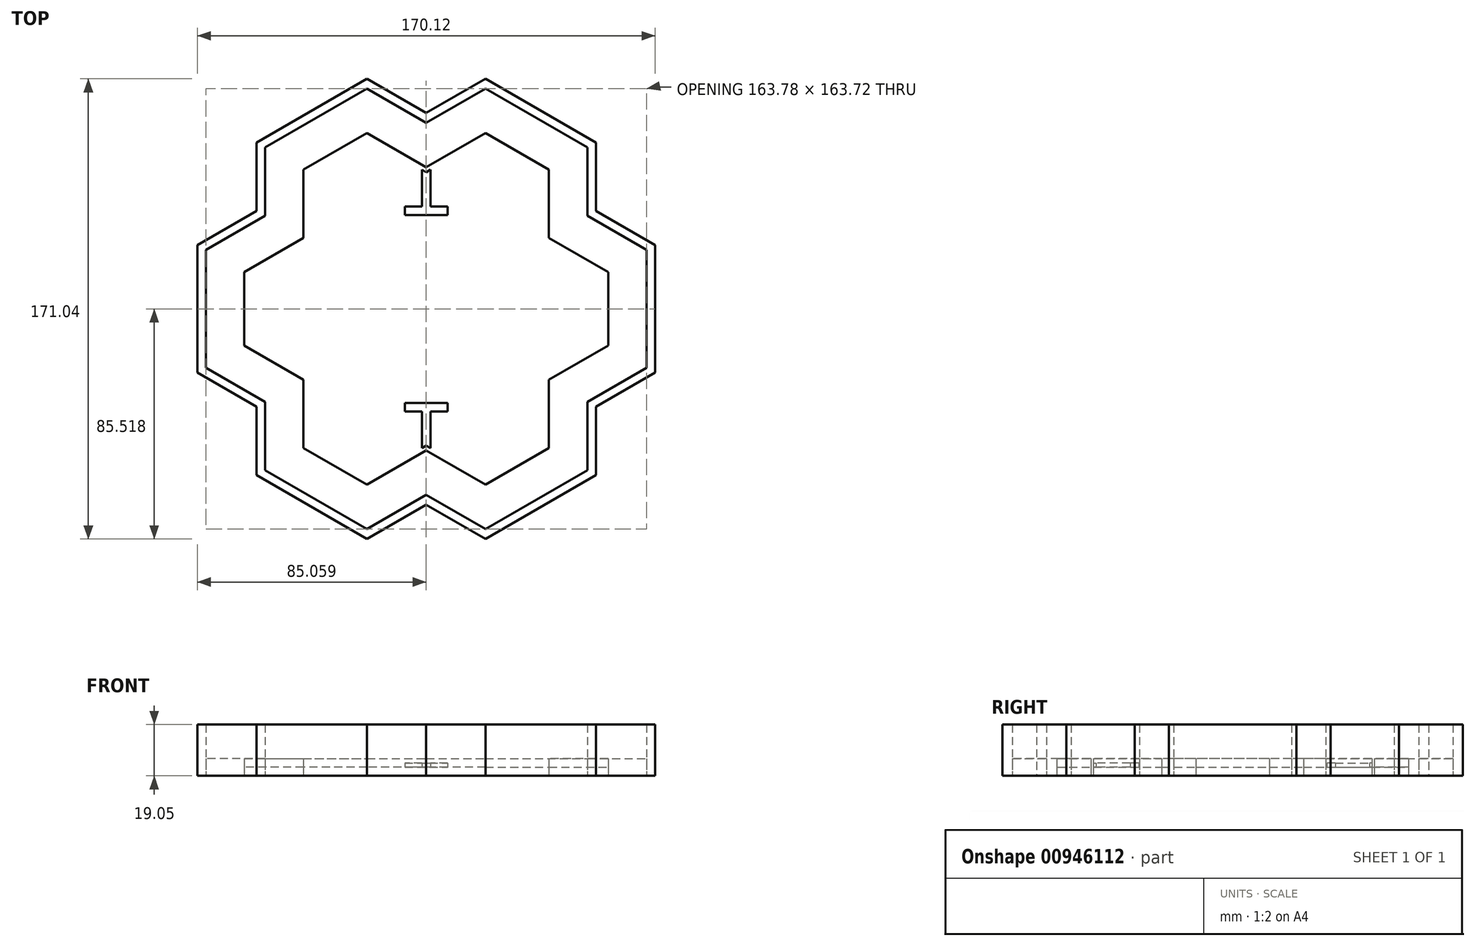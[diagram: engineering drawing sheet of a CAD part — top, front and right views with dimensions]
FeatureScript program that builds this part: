
annotation { "Feature Type Name" : "Feature", "Feature Type Description" : "" }
export const myFeature = defineFeature(function(context is Context, id is Id, definition is map)
    precondition{}
    {
        {
            var Q0;
            Q0=qCreatedBy(makeId("Top.planeOp"),FACE);
            var sketch = newSketch(context, id + "F0", { "sketchPlane" : qUnion([Q0])});
            skLineSegment(sketch, "E0.MirrorCS", {"start": v(-44.94, 24.68) * mm, "end": v(-66.93, 11.98) * mm});
            skLineSegment(sketch, "E1.MirrorCS", {"start": v(-66.93, 11.98) * mm, "end": v(-66.93, -13.42) * mm});
            skLineSegment(sketch, "E2.MirrorCS", {"start": v(-66.93, -13.42) * mm, "end": v(-44.94, -26.12) * mm});
            skLineSegment(sketch, "E3.MirrorCS", {"start": v(-44.94, -26.12) * mm, "end": v(-44.94, -51.52) * mm});
            skLineSegment(sketch, "E4.MirrorCS", {"start": v(-44.94, -51.52) * mm, "end": v(-22.94, -64.22) * mm});
            skLineSegment(sketch, "E5.MirrorCS", {"start": v(-22.94, -64.22) * mm, "end": v(-0.94, -51.52) * mm});
            skLineSegment(sketch, "E6.MirrorCS", {"start": v(-0.94, -51.52) * mm, "end": v(21.06, -64.22) * mm});
            skLineSegment(sketch, "E7.MirrorCS", {"start": v(21.06, -64.22) * mm, "end": v(43.05, -51.52) * mm});
            skLineSegment(sketch, "E8.MirrorCS", {"start": v(43.05, -51.52) * mm, "end": v(43.05, -26.12) * mm});
            skLineSegment(sketch, "E9.MirrorCS", {"start": v(-44.94, 50.08) * mm, "end": v(-44.94, 24.68) * mm});
            skLineSegment(sketch, "E10.MirrorCS", {"start": v(-22.94, 62.78) * mm, "end": v(-44.94, 50.08) * mm});
            skLineSegment(sketch, "E11.MirrorCS", {"start": v(-0.94, 50.08) * mm, "end": v(-22.94, 62.78) * mm});
            skLineSegment(sketch, "E12.MirrorCS", {"start": v(21.06, 62.78) * mm, "end": v(-0.94, 50.08) * mm});
            skLineSegment(sketch, "E13.MirrorCS", {"start": v(43.05, 50.08) * mm, "end": v(21.06, 62.78) * mm});
            skLineSegment(sketch, "E14.MirrorCS", {"start": v(43.05, 24.68) * mm, "end": v(43.05, 50.08) * mm});
            skLineSegment(sketch, "E15.MirrorCS", {"start": v(65.05, 11.98) * mm, "end": v(43.05, 24.68) * mm});
            skLineSegment(sketch, "E16.MirrorCS", {"start": v(65.05, -13.42) * mm, "end": v(65.05, 11.98) * mm});
            skLineSegment(sketch, "E17.MirrorCS", {"start": v(43.05, -26.12) * mm, "end": v(65.05, -13.42) * mm});
            skLineSegment(sketch, "E18.0", {"start": v(-22.94, -66.07) * mm, "end": v(-0.94, -53.37) * mm});
            skLineSegment(sketch, "E18.1", {"start": v(-46.54, -52.45) * mm, "end": v(-22.94, -66.07) * mm});
            skLineSegment(sketch, "E18.2", {"start": v(-46.54, -27.05) * mm, "end": v(-46.54, -52.45) * mm});
            skLineSegment(sketch, "E18.3", {"start": v(-68.53, -14.35) * mm, "end": v(-46.54, -27.05) * mm});
            skLineSegment(sketch, "E18.4", {"start": v(-68.53, 12.9) * mm, "end": v(-68.53, -14.35) * mm});
            skLineSegment(sketch, "E18.5", {"start": v(-0.94, -53.37) * mm, "end": v(21.06, -66.07) * mm});
            skLineSegment(sketch, "E18.6", {"start": v(-46.54, 25.6) * mm, "end": v(-68.53, 12.9) * mm});
            skLineSegment(sketch, "E18.7", {"start": v(-46.54, 51) * mm, "end": v(-46.54, 25.6) * mm});
            skLineSegment(sketch, "E18.8", {"start": v(66.65, -14.35) * mm, "end": v(66.65, 12.9) * mm});
            skLineSegment(sketch, "E18.9", {"start": v(44.65, -27.05) * mm, "end": v(66.65, -14.35) * mm});
            skLineSegment(sketch, "E18.10", {"start": v(44.65, -52.45) * mm, "end": v(44.65, -27.05) * mm});
            skLineSegment(sketch, "E18.11", {"start": v(21.06, -66.07) * mm, "end": v(44.65, -52.45) * mm});
            skLineSegment(sketch, "E18.12", {"start": v(66.65, 12.9) * mm, "end": v(44.65, 25.6) * mm});
            skLineSegment(sketch, "E18.13", {"start": v(44.65, 25.6) * mm, "end": v(44.65, 51) * mm});
            skLineSegment(sketch, "E18.14", {"start": v(44.65, 51) * mm, "end": v(21.06, 64.63) * mm});
            skLineSegment(sketch, "E18.15", {"start": v(21.06, 64.63) * mm, "end": v(-0.94, 51.93) * mm});
            skLineSegment(sketch, "E18.16", {"start": v(-0.94, 51.93) * mm, "end": v(-22.94, 64.63) * mm});
            skLineSegment(sketch, "E18.17", {"start": v(-22.94, 64.63) * mm, "end": v(-46.54, 51) * mm});
            skLineSegment(sketch, "E19.0", {"start": v(-48.14, 26.53) * mm, "end": v(-70.13, 13.83) * mm});
            skLineSegment(sketch, "E19.1", {"start": v(-48.14, 51.93) * mm, "end": v(-48.14, 26.53) * mm});
            skLineSegment(sketch, "E19.2", {"start": v(-22.94, 66.47) * mm, "end": v(-48.14, 51.93) * mm});
            skLineSegment(sketch, "E19.3", {"start": v(-0.94, 53.77) * mm, "end": v(-22.94, 66.47) * mm});
            skLineSegment(sketch, "E19.4", {"start": v(21.06, 66.47) * mm, "end": v(-0.94, 53.77) * mm});
            skLineSegment(sketch, "E19.5", {"start": v(-70.13, 13.83) * mm, "end": v(-70.13, -15.27) * mm});
            skLineSegment(sketch, "E19.6", {"start": v(46.25, 51.93) * mm, "end": v(21.06, 66.47) * mm});
            skLineSegment(sketch, "E19.7", {"start": v(46.25, 26.53) * mm, "end": v(46.25, 51.93) * mm});
            skLineSegment(sketch, "E19.8", {"start": v(-22.94, -67.92) * mm, "end": v(-0.94, -55.22) * mm});
            skLineSegment(sketch, "E19.9", {"start": v(-48.14, -53.37) * mm, "end": v(-22.94, -67.92) * mm});
            skLineSegment(sketch, "E19.10", {"start": v(-48.14, -27.97) * mm, "end": v(-48.14, -53.37) * mm});
            skLineSegment(sketch, "E19.11", {"start": v(-70.13, -15.27) * mm, "end": v(-48.14, -27.97) * mm});
            skLineSegment(sketch, "E19.12", {"start": v(-0.94, -55.22) * mm, "end": v(21.06, -67.92) * mm});
            skLineSegment(sketch, "E19.13", {"start": v(21.06, -67.92) * mm, "end": v(46.25, -53.37) * mm});
            skLineSegment(sketch, "E19.14", {"start": v(46.25, -53.37) * mm, "end": v(46.25, -27.97) * mm});
            skLineSegment(sketch, "E19.15", {"start": v(46.25, -27.97) * mm, "end": v(68.25, -15.27) * mm});
            skLineSegment(sketch, "E19.16", {"start": v(68.25, -15.27) * mm, "end": v(68.25, 13.83) * mm});
            skLineSegment(sketch, "E19.17", {"start": v(68.25, 13.83) * mm, "end": v(46.25, 26.53) * mm});
            skLineSegment(sketch, "E20.0", {"start": v(-22.94, 81.14) * mm, "end": v(-60.84, 59.26) * mm});
            skLineSegment(sketch, "E20.1", {"start": v(-0.94, 68.44) * mm, "end": v(-22.94, 81.14) * mm});
            skLineSegment(sketch, "E20.2", {"start": v(21.06, 81.14) * mm, "end": v(-0.94, 68.44) * mm});
            skLineSegment(sketch, "E20.3", {"start": v(58.95, 59.26) * mm, "end": v(21.06, 81.14) * mm});
            skLineSegment(sketch, "E20.4", {"start": v(58.95, 33.86) * mm, "end": v(58.95, 59.26) * mm});
            skLineSegment(sketch, "E20.5", {"start": v(-60.84, 59.26) * mm, "end": v(-60.84, 33.86) * mm});
            skLineSegment(sketch, "E20.6", {"start": v(80.95, 21.16) * mm, "end": v(58.95, 33.86) * mm});
            skLineSegment(sketch, "E20.7", {"start": v(80.95, -22.6) * mm, "end": v(80.95, 21.16) * mm});
            skLineSegment(sketch, "E20.8", {"start": v(-60.84, -35.3) * mm, "end": v(-60.84, -60.7) * mm});
            skLineSegment(sketch, "E20.9", {"start": v(-82.83, -22.6) * mm, "end": v(-60.84, -35.3) * mm});
            skLineSegment(sketch, "E20.10", {"start": v(-82.83, 21.16) * mm, "end": v(-82.83, -22.6) * mm});
            skLineSegment(sketch, "E20.11", {"start": v(-60.84, 33.86) * mm, "end": v(-82.83, 21.16) * mm});
            skLineSegment(sketch, "E20.12", {"start": v(-60.84, -60.7) * mm, "end": v(-22.94, -82.58) * mm});
            skLineSegment(sketch, "E20.13", {"start": v(-22.94, -82.58) * mm, "end": v(-0.94, -69.88) * mm});
            skLineSegment(sketch, "E20.14", {"start": v(-0.94, -69.88) * mm, "end": v(21.06, -82.58) * mm});
            skLineSegment(sketch, "E20.15", {"start": v(21.06, -82.58) * mm, "end": v(58.95, -60.7) * mm});
            skLineSegment(sketch, "E20.16", {"start": v(58.95, -60.7) * mm, "end": v(58.95, -35.3) * mm});
            skLineSegment(sketch, "E20.17", {"start": v(58.95, -35.3) * mm, "end": v(80.95, -22.6) * mm});
            skLineSegment(sketch, "E21.0", {"start": v(-64, 35.69) * mm, "end": v(-86, 22.99) * mm});
            skLineSegment(sketch, "E21.1", {"start": v(-64, 61.09) * mm, "end": v(-64, 35.69) * mm});
            skLineSegment(sketch, "E21.2", {"start": v(-22.94, 84.8) * mm, "end": v(-64, 61.09) * mm});
            skLineSegment(sketch, "E21.3", {"start": v(-0.94, 72.1) * mm, "end": v(-22.94, 84.8) * mm});
            skLineSegment(sketch, "E21.4", {"start": v(21.06, 84.8) * mm, "end": v(-0.94, 72.1) * mm});
            skLineSegment(sketch, "E21.5", {"start": v(-86, 22.99) * mm, "end": v(-86, -24.43) * mm});
            skLineSegment(sketch, "E21.6", {"start": v(62.12, 61.09) * mm, "end": v(21.06, 84.8) * mm});
            skLineSegment(sketch, "E21.7", {"start": v(62.12, 35.69) * mm, "end": v(62.12, 61.09) * mm});
            skLineSegment(sketch, "E21.8", {"start": v(-22.94, -86.24) * mm, "end": v(-0.94, -73.54) * mm});
            skLineSegment(sketch, "E21.9", {"start": v(-64, -62.53) * mm, "end": v(-22.94, -86.24) * mm});
            skLineSegment(sketch, "E21.10", {"start": v(-64, -37.13) * mm, "end": v(-64, -62.53) * mm});
            skLineSegment(sketch, "E21.11", {"start": v(-86, -24.43) * mm, "end": v(-64, -37.13) * mm});
            skLineSegment(sketch, "E21.12", {"start": v(-0.94, -73.54) * mm, "end": v(21.06, -86.24) * mm});
            skLineSegment(sketch, "E21.13", {"start": v(21.06, -86.24) * mm, "end": v(62.12, -62.53) * mm});
            skLineSegment(sketch, "E21.14", {"start": v(62.12, -62.53) * mm, "end": v(62.12, -37.13) * mm});
            skLineSegment(sketch, "E21.15", {"start": v(62.12, -37.13) * mm, "end": v(84.12, -24.43) * mm});
            skLineSegment(sketch, "E21.16", {"start": v(84.12, -24.43) * mm, "end": v(84.12, 22.99) * mm});
            skLineSegment(sketch, "E21.17", {"start": v(84.12, 22.99) * mm, "end": v(62.12, 35.69) * mm});
            skLineSegment(sketch, "E22.0", {"start": v(-2.54, 50.08) * mm, "end": v(-2.54, 37.38) * mm});
            skLineSegment(sketch, "E23.0", {"start": v(0.66, 50.08) * mm, "end": v(0.66, 37.38) * mm});
            skLineSegment(sketch, "E24", {"start": v(0.66, 37.38) * mm, "end": v(-2.54, 37.38) * mm});
            skLineSegment(sketch, "E25.0", {"start": v(0.66, -51.52) * mm, "end": v(0.66, -38.82) * mm});
            skLineSegment(sketch, "E26.0", {"start": v(-2.54, -51.52) * mm, "end": v(-2.54, -38.82) * mm});
            skLineSegment(sketch, "E27", {"start": v(-2.54, -51.52) * mm, "end": v(-2.54, -52.45) * mm});
            skLineSegment(sketch, "E28", {"start": v(0.66, -51.52) * mm, "end": v(0.66, -52.45) * mm});
            skLineSegment(sketch, "E29", {"start": v(-2.54, -38.82) * mm, "end": v(0.66, -38.82) * mm});
            skLineSegment(sketch, "E30", {"start": v(-2.54, 50.08) * mm, "end": v(-2.54, 51) * mm});
            skLineSegment(sketch, "E31", {"start": v(0.66, 50.08) * mm, "end": v(0.66, 51) * mm});
            skLineSegment(sketch, "E32", {"start": v(-2.54, 37.38) * mm, "end": v(-8.9, 37.38) * mm});
            skLineSegment(sketch, "E33", {"start": v(-8.9, 37.38) * mm, "end": v(-8.9, 34.2) * mm});
            skLineSegment(sketch, "E34", {"start": v(-8.9, 34.2) * mm, "end": v(7, 34.2) * mm});
            skLineSegment(sketch, "E35", {"start": v(7, 34.2) * mm, "end": v(7, 37.38) * mm});
            skLineSegment(sketch, "E36", {"start": v(7, 37.38) * mm, "end": v(0.66, 37.38) * mm});
            skLineSegment(sketch, "E37", {"start": v(-2.54, -38.82) * mm, "end": v(-8.9, -38.82) * mm});
            skLineSegment(sketch, "E38", {"start": v(-8.9, -38.82) * mm, "end": v(-8.9, -35.65) * mm});
            skLineSegment(sketch, "E39", {"start": v(-8.9, -35.65) * mm, "end": v(7, -35.65) * mm});
            skLineSegment(sketch, "E40", {"start": v(7, -35.65) * mm, "end": v(7, -38.82) * mm});
            skLineSegment(sketch, "E41", {"start": v(7, -38.82) * mm, "end": v(0.66, -38.82) * mm});
            skSolve(sketch);
        }
        {
            var Q0;
            Q0=makeQuery(id+"F0.imprint","IMPRINT",FACE,{"disambiguationData":[TD([[makeQuery(id+"F0.imprint","IMPRINT",EDGE,{"derivedFrom":sQuery(id+"F0.wireOp",EDGE,"E18.0")}),-1.0]])]});
            var Q1;
            Q1=makeQuery(id+"F0.imprint","IMPRINT",FACE,{"disambiguationData":[TD([[makeQuery(id+"F0.imprint","IMPRINT",EDGE,{"derivedFrom":sQuery(id+"F0.wireOp",EDGE,"E19.0")}),-1.0]])]});
            extrude(context, id + "F1", {"entities" : qUnion([Q0, Q1]), "depth" : 6.35 * mm, "offsetDistance" : 25.4 * mm});
        }
        {
            var Q0;
            Q0=makeQuery(id+"F0.imprint","IMPRINT",FACE,{"disambiguationData":[TD([[makeQuery(id+"F0.imprint","IMPRINT",EDGE,{"derivedFrom":sQuery(id+"F0.wireOp",EDGE,"E20.0")}),-1.0]])]});
            extrude(context, id + "F2", {"entities" : qUnion([Q0]), "depth" : 19.05 * mm, "offsetDistance" : 25.4 * mm});
        }
        {
            var Q0;
            Q0=makeQuery(id+"F0.imprint","IMPRINT",FACE,{"disambiguationData":[TD([[makeQuery(id+"F0.imprint","IMPRINT",EDGE,{"derivedFrom":sQuery(id+"F0.wireOp",EDGE,"E0.MirrorCS")}),1.0]])]});
            var Q1;
            Q1=makeQuery(id+"F0.imprint","IMPRINT",FACE,{"disambiguationData":[TD([[makeQuery(id+"F0.imprint","IMPRINT",EDGE,{"derivedFrom":sQuery(id+"F0.wireOp",EDGE,"E0.MirrorCS")}),-1.0]])]});
            extrude(context, id + "F3", {"entities" : qUnion([Q0, Q1]), "depth" : 3.17 * mm, "offsetDistance" : 25.4 * mm});
        }
        {
            var Q0;
            Q0=makeQuery(id+"F0.imprint","IMPRINT",FACE,{"disambiguationData":[TD([[makeQuery(id+"F0.imprint","IMPRINT",EDGE,{"derivedFrom":sQuery(id+"F0.wireOp",EDGE,"E24")}),1.0]])]});
            var Q1;
            Q1=makeQuery(id+"F0.imprint","IMPRINT",FACE,{"disambiguationData":[TD([[makeQuery(id+"F0.imprint","IMPRINT",EDGE,{"derivedFrom":sQuery(id+"F0.wireOp",EDGE,"E22.0")}),1.0]])]});
            var Q2;
            Q2=makeQuery(id+"F0.imprint","IMPRINT",FACE,{"disambiguationData":[TD([[makeQuery(id+"F0.imprint","IMPRINT",EDGE,{"derivedFrom":sQuery(id+"F0.wireOp",EDGE,"E25.0")}),1.0]])]});
            var Q3;
            Q3=makeQuery(id+"F0.imprint","IMPRINT",FACE,{"disambiguationData":[TD([[makeQuery(id+"F0.imprint","IMPRINT",EDGE,{"derivedFrom":sQuery(id+"F0.wireOp",EDGE,"E29")}),1.0]])]});
            extrude(context, id + "F4", {"entities" : qUnion([Q0, Q1, Q2, Q3]), "operationType" : NewBodyOperationType.ADD, "depth" : 4.78 * mm, "offsetDistance" : 25.4 * mm});
        }
    });
